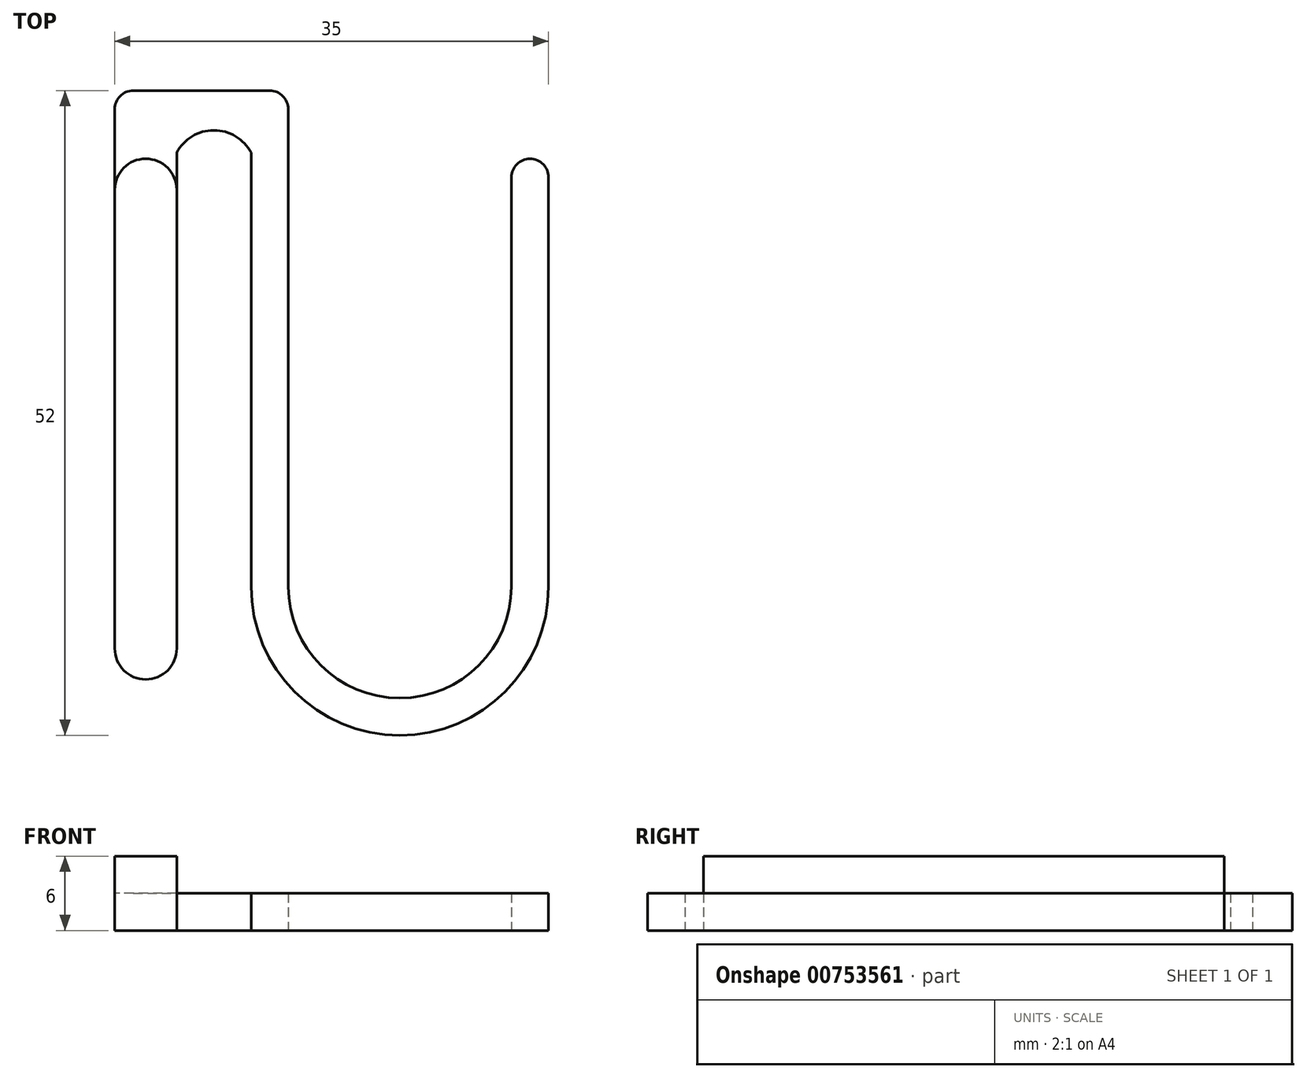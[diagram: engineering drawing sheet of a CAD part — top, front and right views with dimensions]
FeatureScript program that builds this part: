
annotation { "Feature Type Name" : "Feature", "Feature Type Description" : "" }
export const myFeature = defineFeature(function(context is Context, id is Id, definition is map)
    precondition{}
    {
        {
            var Q0;
            Q0=qCreatedBy(makeId("Top.planeOp"),FACE);
            var sketch = newSketch(context, id + "F0", { "sketchPlane" : qUnion([Q0])});
            skArc(sketch, "E0", {"start": v(-9, 0) * mm, "mid": v(0, -9) * mm, "end": v(9, 0) * mm});
            skLineSegment(sketch, "E1", {"start": v(9, 0) * mm, "end": v(9, 33) * mm});
            skArc(sketch, "E2.1", {"start": v(-12, 0) * mm, "mid": v(0, -12) * mm, "end": v(12, 0) * mm});
            skLineSegment(sketch, "E2.2", {"start": v(12, 0) * mm, "end": v(12, 33) * mm});
            skArc(sketch, "E3", {"start": v(9, 33) * mm, "mid": v(10.5, 34.5) * mm, "end": v(12, 33) * mm});
            skLineSegment(sketch, "E4", {"start": v(9, 33) * mm, "end": v(12, 33) * mm, "construction": true});
            skLineSegment(sketch, "E5", {"start": v(-18, 35) * mm, "end": v(-18, -5) * mm});
            skLineSegment(sketch, "E6", {"start": v(-23, -5) * mm, "end": v(-23, 40) * mm});
            skArc(sketch, "E7", {"start": v(-23, -5) * mm, "mid": v(-20.5, -7.5) * mm, "end": v(-18, -5) * mm});
            skArc(sketch, "E8", {"start": v(-12, 35) * mm, "mid": v(-15, 36.8) * mm, "end": v(-18, 35) * mm});
            skLineSegment(sketch, "E9", {"start": v(-23, 40) * mm, "end": v(-9, 40) * mm});
            skLineSegment(sketch, "E10", {"start": v(-12, 0) * mm, "end": v(-12, 35) * mm});
            skLineSegment(sketch, "E11", {"start": v(-12, 0) * mm, "end": v(12, 0) * mm, "construction": true});
            skLineSegment(sketch, "E12", {"start": v(-9, 0) * mm, "end": v(-9, 40) * mm});
            skLineSegment(sketch, "E13", {"start": v(-18, 35) * mm, "end": v(-12, 35) * mm, "construction": true});
            skSolve(sketch);
        }
        {
            var Q0;
            Q0=makeQuery(id+"F0.imprint","IMPRINT",FACE,{"disambiguationData":[TD([[makeQuery(id+"F0.imprint","IMPRINT",EDGE,{"derivedFrom":sQuery(id+"F0.wireOp",EDGE,"E0")}),-1.0]])]});
            extrude(context, id + "F1", {"entities" : qUnion([Q0]), "depth" : 3 * mm, "offsetDistance" : 25 * mm});
        }
        {
            var Q0;
            Q0=makeQuery(id+"F1.opExtrude","CAP_FACE",FACE,{"disambiguationData":[OSD([sQuery(id+"F0.wireOp",EDGE,"E0"),sQuery(id+"F0.wireOp",EDGE,"7QnvPKYh-SZPt-ygPD-fNfa-oWlKRZie6YXf"),sQuery(id+"F0.wireOp",EDGE,"E1"),sQuery(id+"F0.wireOp",EDGE,"E2.0"),sQuery(id+"F0.wireOp",EDGE,"E2.1"),sQuery(id+"F0.wireOp",EDGE,"E2.2"),sQuery(id+"F0.wireOp",EDGE,"E3"),sQuery(id+"F0.wireOp",EDGE,"E5"),sQuery(id+"F0.wireOp",EDGE,"E6"),sQuery(id+"F0.wireOp",EDGE,"E7"),sQuery(id+"F0.wireOp",EDGE,"E8"),sQuery(id+"F0.wireOp",EDGE,"E9")])],"isStart":false});
            var sketch = newSketch(context, id + "F2", { "sketchPlane" : qUnion([Q0])});
            skLineSegment(sketch, "E14", {"start": v(-23, 32) * mm, "end": v(-18, 32) * mm, "construction": true});
            skArc(sketch, "E15", {"start": v(-18, 32) * mm, "mid": v(-20.5, 34.5) * mm, "end": v(-23, 32) * mm});
            skSolve(sketch);
        }
        {
            var Q0;
            {var subQ0=sQuery(id+"F2.wireOp",EDGE,"E15");Q0=makeQuery(id+"F2.imprint","IMPRINT",FACE,{"disambiguationData":[TD([[makeQuery(id+"F2.imprint","IMPRINT",EDGE,{"derivedFrom":subQ0}),1.0]])]});}
            extrude(context, id + "F3", {"entities" : qUnion([Q0]), "operationType" : NewBodyOperationType.ADD, "depth" : 3 * mm, "offsetDistance" : 25 * mm});
        }
        {
            var Q0;
            Q0=makeQuery(id+"F1.opExtrude","SWEPT_EDGE",EDGE,{"disambiguationData":[OSD([sQuery(id+"F0.wireOp",EDGE,"7QnvPKYh-SZPt-ygPD-fNfa-oWlKRZie6YXf"),sQuery(id+"F0.wireOp",EDGE,"E9")])]});
            var Q1;
            Q1=makeQuery(id+"F1.opExtrude","SWEPT_EDGE",EDGE,{"disambiguationData":[OSD([sQuery(id+"F0.wireOp",EDGE,"E6"),sQuery(id+"F0.wireOp",EDGE,"E9")])]});
            fillet(context, id + "F4", {"entities" : qUnion([Q0, Q1]), "radius" : 1.5 * mm, "tangentPropagation" : true, "allowEdgeOverflow" : false});
        }
    });
